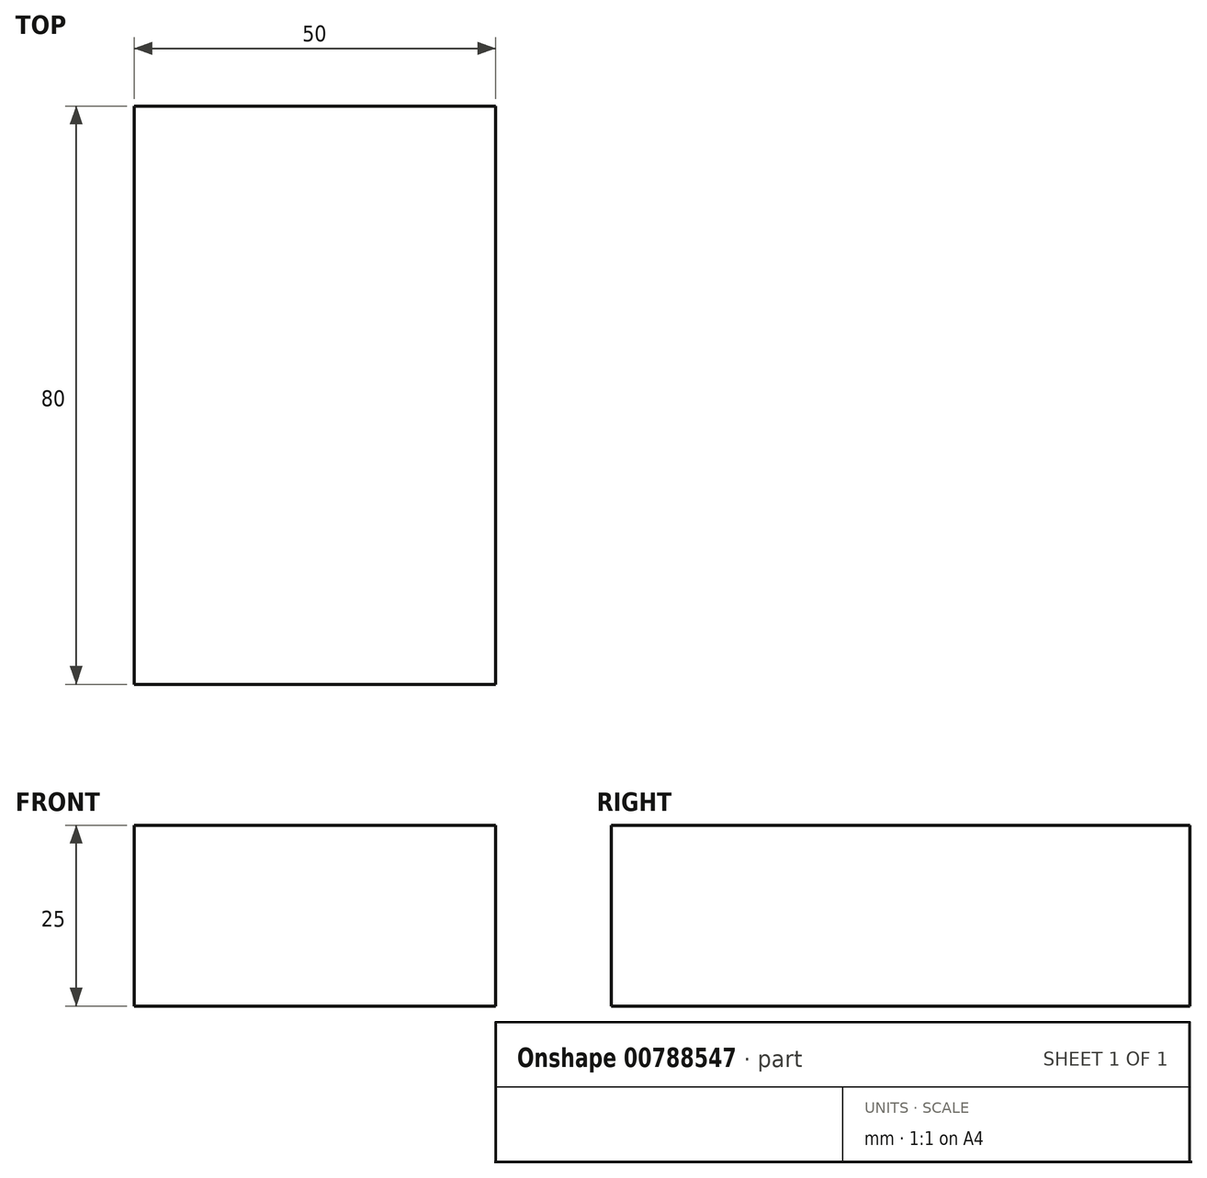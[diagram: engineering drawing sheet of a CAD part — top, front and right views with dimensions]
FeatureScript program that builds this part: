
annotation { "Feature Type Name" : "Feature", "Feature Type Description" : "" }
export const myFeature = defineFeature(function(context is Context, id is Id, definition is map)
    precondition{}
    {
        {
            var Q0;
            Q0=qCreatedBy(makeId("Top.planeOp"),FACE);
            var sketch = newSketch(context, id + "F0", { "sketchPlane" : qUnion([Q0])});
            skLineSegment(sketch, "E0.bottom", {"start": v(-25, 40) * mm, "end": v(25, 40) * mm});
            skLineSegment(sketch, "E0.top", {"start": v(-25, -40) * mm, "end": v(25, -40) * mm});
            skLineSegment(sketch, "E0.left", {"start": v(-25, 40) * mm, "end": v(-25, -40) * mm});
            skLineSegment(sketch, "E0.right", {"start": v(25, 40) * mm, "end": v(25, -40) * mm});
            skPoint(sketch, "E0.middle", {"position": v(0, 0) * mm});
            skSolve(sketch);
        }
        {
            var Q0;
            Q0 = qSketchRegion(id + "F0", true);
            extrude(context, id + "F1", {"entities" : qUnion([Q0]), "depth" : 25 * mm, "offsetDistance" : 25 * mm});
        }
    });
